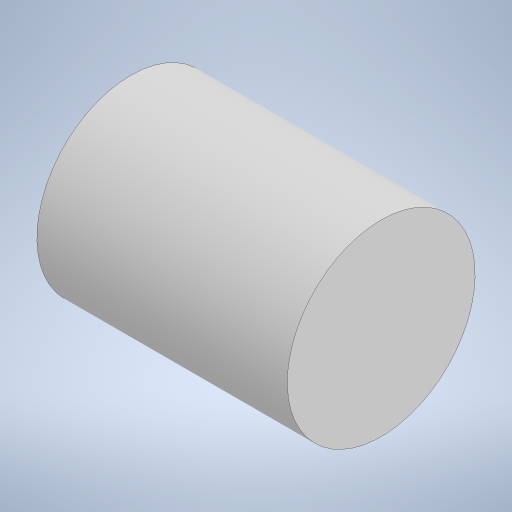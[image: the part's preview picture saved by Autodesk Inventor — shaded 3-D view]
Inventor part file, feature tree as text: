
AUTODESK INVENTOR PART (.ipt)
format: ipt  version: 2023 (Build 270158030, 158C)  size: 190,976 bytes
history: native  units: in
note: dims shown in document units (in); Inventor stores cm internally (conversion verified against a paired STEP export)
features: extrude x1, sketch x1
ambient origin geometry x8: Origin, YZ Plane, XZ Plane, XY Plane, X Axis, Y Axis, Z Axis, Center Point
bodies: Solid1 (feature_tree)
feature tree (2):
  extrude  "Extrusion1"  Depth=1.0in TaperAngle=0.0deg
  sketch  "Sketch1"  dims[d0=0.75in d1=1.0in d2=0.0in]
